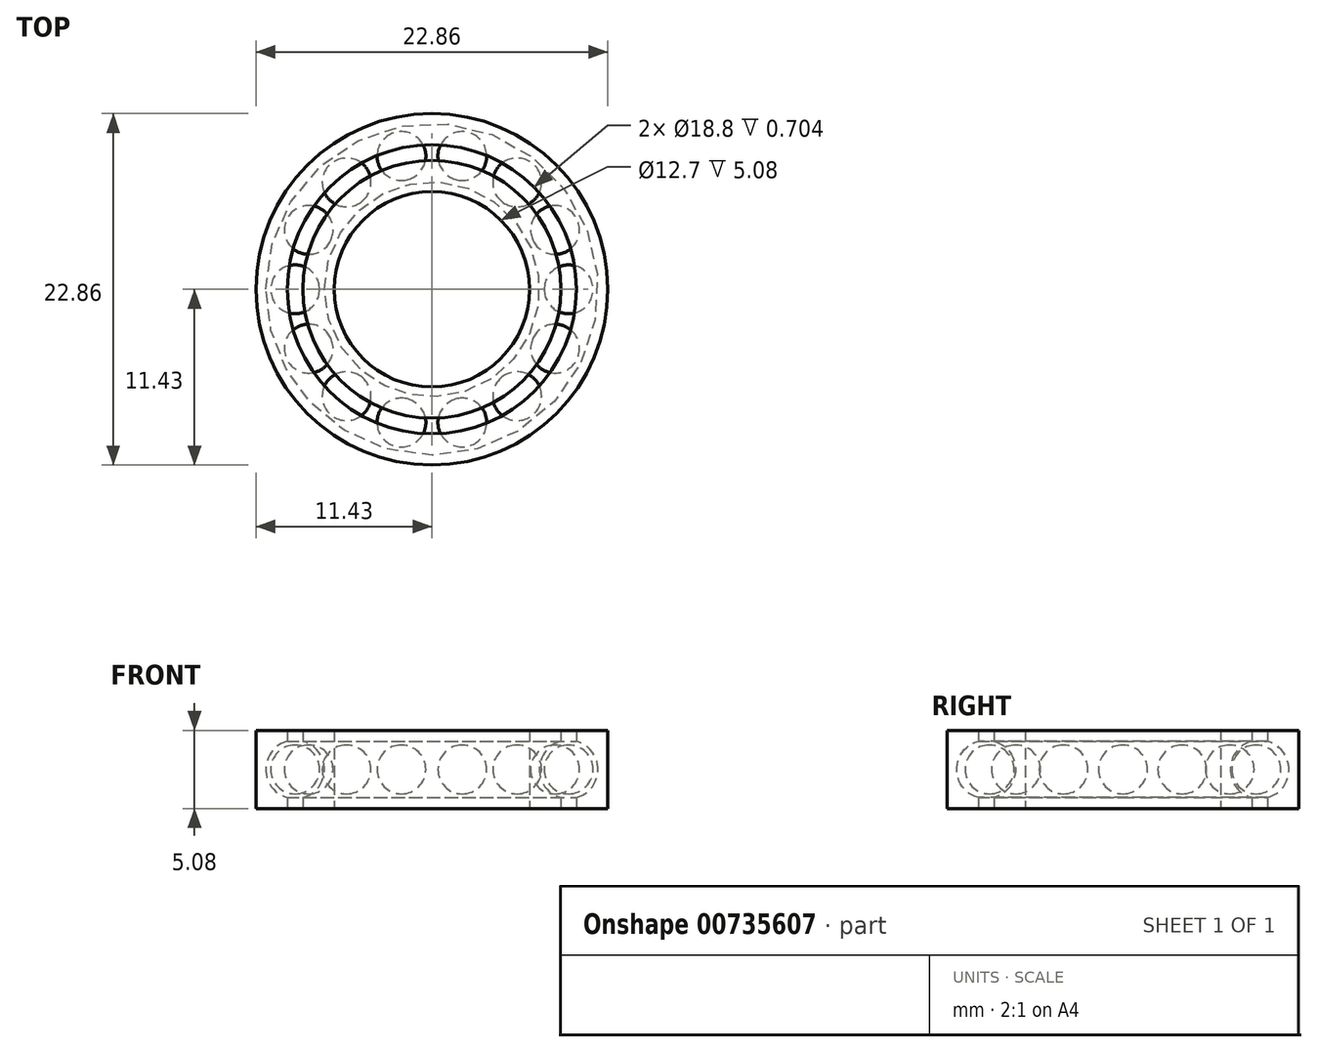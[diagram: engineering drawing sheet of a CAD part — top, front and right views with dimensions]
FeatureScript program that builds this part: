
annotation { "Feature Type Name" : "Feature", "Feature Type Description" : "" }
export const myFeature = defineFeature(function(context is Context, id is Id, definition is map)
    precondition{}
    {
        {
            var Q0;
            Q0=qCreatedBy(makeId("Front.planeOp"),FACE);
            var sketch = newSketch(context, id + "F0", { "sketchPlane" : qUnion([Q0])});
            skPoint(sketch, "E0", {"position": v(-6.35, 0) * mm});
            skLineSegment(sketch, "E1", {"start": v(-6.35, 0) * mm, "end": v(-6.35, 2.54) * mm});
            skLineSegment(sketch, "E2.MirrorCS", {"start": v(-6.35, 0) * mm, "end": v(-6.35, -2.54) * mm});
            skLineSegment(sketch, "E3", {"start": v(-6.35, 2.54) * mm, "end": v(-8.38, 2.54) * mm});
            skLineSegment(sketch, "E4", {"start": v(-6.35, -2.54) * mm, "end": v(-8.38, -2.54) * mm});
            skArc(sketch, "E5", {"start": v(-9.4, 1.84) * mm, "mid": v(-10.8, 0) * mm, "end": v(-9.4, -1.84) * mm});
            skLineSegment(sketch, "E6", {"start": v(-6.35, 2.54) * mm, "end": v(-6.35, -2.54) * mm});
            skPoint(sketch, "E7", {"position": v(-6.99, 1.9) * mm});
            skPoint(sketch, "E8.MirrorP", {"position": v(-6.99, -1.9) * mm});
            skLineSegment(sketch, "E9", {"start": v(-8.9, 1.59) * mm, "end": v(-8.9, -1.59) * mm});
            skCircle(sketch, "E10", {"center": v(-8.9, 0) * mm, "radius": 1.59 * mm});
            skLineSegment(sketch, "E11", {"start": v(-9.4, 2.54) * mm, "end": v(-9.4, 1.84) * mm});
            skLineSegment(sketch, "E12", {"start": v(-8.38, 2.54) * mm, "end": v(-8.38, 1.84) * mm});
            skPoint(sketch, "E13.MirrorCS.start.orphan", {"position": v(-8.9, 2.9) * mm});
            skArc(sketch, "E14.trimOffspring", {"start": v(-8.38, -1.84) * mm, "mid": v(-6.99, 0) * mm, "end": v(-8.38, 1.84) * mm});
            skLineSegment(sketch, "E15", {"start": v(-11.43, 2.54) * mm, "end": v(-11.43, -2.54) * mm});
            skPoint(sketch, "E16.orphan", {"position": v(-9.4, 2.9) * mm});
            skPoint(sketch, "E17.orphan", {"position": v(-8.38, 2.9) * mm});
            skLineSegment(sketch, "E18.trimOffspring", {"start": v(-9.4, 2.54) * mm, "end": v(-11.43, 2.54) * mm});
            skLineSegment(sketch, "E19.trimOffspring", {"start": v(-9.4, -2.54) * mm, "end": v(-11.43, -2.54) * mm});
            skLineSegment(sketch, "E20.trimOffspring", {"start": v(-9.4, -1.84) * mm, "end": v(-9.4, -2.54) * mm});
            skLineSegment(sketch, "E21.trimOffspring", {"start": v(-8.38, -1.84) * mm, "end": v(-8.38, -2.54) * mm});
            skLineSegment(sketch, "E22", {"start": v(0, -2.21) * mm, "end": v(0, 2.77) * mm});
            skSolve(sketch);
        }
        {
            var Q0;
            Q0=makeQuery(id+"F0.imprint","IMPRINT",FACE,{"disambiguationData":[TD([[makeQuery(id+"F0.imprint","IMPRINT",EDGE,{"derivedFrom":sQuery(id+"F0.wireOp",EDGE,"E5")}),-1.0]])]});
            var Q1;
            Q1=makeQuery(id+"F0.imprint","IMPRINT",FACE,{"disambiguationData":[TD([[makeQuery(id+"F0.imprint","IMPRINT",EDGE,{"derivedFrom":sQuery(id+"F0.wireOp",EDGE,"E3")}),1.0]])]});
            var Q2;
            Q2=sQuery(id+"F0.wireOp",EDGE,"E22");
            revolve(context, id + "F1", {"surfaceOperationType" : NewSurfaceOperationType.NEW, "entities" : qUnion([Q0, Q1]), "axis" : qUnion([Q2]), "revolveType" : RevolveType.FULL});
        }
        {
            var Q0;
            {var subQ0=sQuery(id+"F0.wireOp",EDGE,"E9");Q0=makeQuery(id+"F0.imprint","IMPRINT",FACE,{"disambiguationData":[TD([[makeQuery(id+"F0.imprint","IMPRINT",EDGE,{"derivedFrom":subQ0}),1.0]])]});}
            var Q1;
            Q1=sQuery(id+"F0.wireOp",EDGE,"E9");
            revolve(context, id + "F2", {"surfaceOperationType" : NewSurfaceOperationType.NEW, "entities" : qUnion([Q0]), "axis" : qUnion([Q1]), "revolveType" : RevolveType.FULL});
        }
        {
            var Q0;
            Q0=makeQuery(id+"F2.opRevolve","SWEPT_BODY",BODY,{"disambiguationData":[OSD([sQuery(id+"F0.wireOp",EDGE,"E9"),sQuery(id+"F0.wireOp",EDGE,"E10")])]});
            var Q1;
            Q1=sQuery(id+"F0.wireOp",EDGE,"E22");
            circularPattern(context, id + "F3", {"entities" : qUnion([Q0]), "axis" : qUnion([Q1]), "angle" : 360 * degree, "instanceCount" : 14, "equalSpace" : true});
        }
    });
